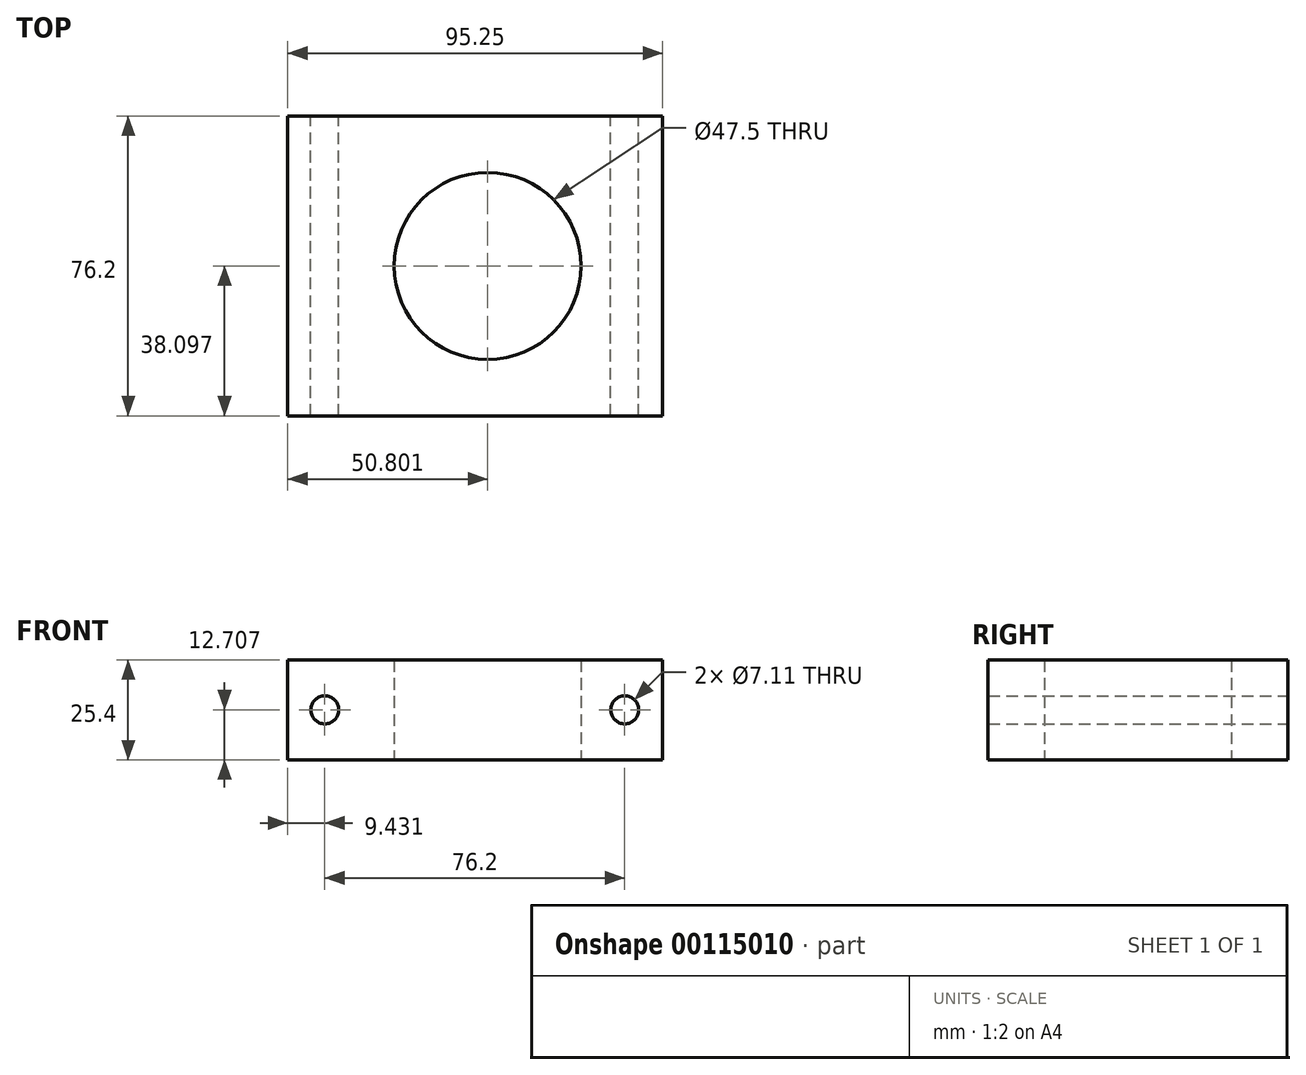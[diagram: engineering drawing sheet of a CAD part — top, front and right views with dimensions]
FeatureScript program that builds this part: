
annotation { "Feature Type Name" : "Feature", "Feature Type Description" : "" }
export const myFeature = defineFeature(function(context is Context, id is Id, definition is map)
    precondition{}
    {
        {
            var Q0;
            Q0=qCreatedBy(makeId("Top.planeOp"),FACE);
            var sketch = newSketch(context, id + "F0", { "sketchPlane" : qUnion([Q0])});
            skLineSegment(sketch, "E0.bottom", {"start": v(-29.2, 45.86) * mm, "end": v(66.05, 45.86) * mm});
            skLineSegment(sketch, "E0.top", {"start": v(-29.2, -30.34) * mm, "end": v(66.05, -30.34) * mm});
            skLineSegment(sketch, "E0.left", {"start": v(-29.2, 45.86) * mm, "end": v(-29.2, -30.34) * mm});
            skLineSegment(sketch, "E0.right", {"start": v(66.05, 45.86) * mm, "end": v(66.05, -30.34) * mm});
            skCircle(sketch, "E1", {"center": v(21.6, 7.76) * mm, "radius": 23.75 * mm});
            skLineSegment(sketch, "E2", {"start": v(-29.2, 7.76) * mm, "end": v(-2.15, 7.76) * mm});
            skLineSegment(sketch, "E3.trimOffspring", {"start": v(45.35, 7.76) * mm, "end": v(66.05, 7.76) * mm});
            skSolve(sketch);
        }
        {
            var Q0;
            {var subQ4=sQuery(id+"F0.wireOp",EDGE,"E0.top");Q0=makeQuery(id+"F0.imprint","IMPRINT",FACE,{"disambiguationData":[TD([[makeQuery(id+"F0.imprint","IMPRINT",EDGE,{"derivedFrom":subQ4}),1.0]])]});}
            var Q1;
            {var subQ4=sQuery(id+"F0.wireOp",EDGE,"E0.bottom");Q1=makeQuery(id+"F0.imprint","IMPRINT",FACE,{"disambiguationData":[TD([[makeQuery(id+"F0.imprint","IMPRINT",EDGE,{"derivedFrom":subQ4}),-1.0]])]});}
            extrude(context, id + "F1", {"entities" : qUnion([Q0, Q1]), "depth" : 25.4 * mm});
        }
        {
            var Q0;
            Q0=qCreatedBy(makeId("Front.planeOp"),FACE);
            var sketch = newSketch(context, id + "F2", { "sketchPlane" : qUnion([Q0])});
            skCircle(sketch, "E4", {"center": v(-19.77, 12.7) * mm, "radius": 3.56 * mm});
            skCircle(sketch, "E5", {"center": v(56.43, 12.7) * mm, "radius": 3.56 * mm});
            skSolve(sketch);
        }
        {
            var Q0;
            Q0 = qSketchRegion(id + "F2", true);
            var Q1;
            Q1=makeQuery(id+"F1.opExtrude","SWEPT_FACE",FACE,{"disambiguationData":[OSD([sQuery(id+"F0.wireOp",EDGE,"E0.top")])]});
            extrude(context, id + "F3", {"entities" : qUnion([Q0]), "operationType" : NewBodyOperationType.REMOVE, "endBound" : BoundingType.UP_TO_SURFACE, "endBoundEntityFace" : qUnion([Q1]), "depth" : 25.4 * mm});
        }
        {
            var Q0;
            Q0=makeQuery(id+"F3.boolean.opBoolean","COPY",FACE,{"derivedFrom":makeQuery(id+"F3.opExtrude","CAP_FACE",FACE,{"disambiguationData":[OSD([sQuery(id+"F2.wireOp",EDGE,"E4")])],"isStart":true})});
            var Q1;
            Q1=makeQuery(id+"F3.boolean.opBoolean","COPY",FACE,{"derivedFrom":makeQuery(id+"F3.opExtrude","CAP_FACE",FACE,{"disambiguationData":[OSD([sQuery(id+"F2.wireOp",EDGE,"E5")])],"isStart":true})});
            var Q2;
            Q2=makeQuery(id+"F1.opExtrude","SWEPT_FACE",FACE,{"disambiguationData":[OSD([sQuery(id+"F0.wireOp",EDGE,"E0.bottom")])]});
            extrude(context, id + "F4", {"entities" : qUnion([Q0, Q1]), "operationType" : NewBodyOperationType.REMOVE, "endBound" : BoundingType.UP_TO_SURFACE, "oppositeDirection" : true, "endBoundEntityFace" : qUnion([Q2]), "depth" : 25.4 * mm});
        }
    });
